# Revit family: Haworth_Morrison_Stool
name_source: partatom
category: Furniture
revit_build: Autodesk Revit 2018 (Build: 20170223_1515(x64)
units: mm (PartAtom-declared; Revit-internal decimal feet)

## family parameters
Always vertical = Yes
Cut with Voids When Loaded = No
OmniClass Number = 23.40.70.14.64.21
OmniClass Title = Systems Furniture
Room Calculation Point = No
Shared = No
Work Plane-Based = No

## types (3) — shared parameters
Actual Depth = 13 3/4"
Actual Width = 17 1/4"
Assembly Code = E2020200
Glide Finish = Haworth _ Polymer _ Slate
Manufacturer = Haworth
Model = HCCE-MSS
Revision Number = 7
Size = Verify Final Dim. w/ Haworth
URL = http://www.haworth.com
URL - Product = http://www.haworth.com
Warranty = http://www.haworth.com

## per-type parameters (varying)
| type | Actual Height | Description | High | Low | Medium | Seat Height |
| HCCE-MSS3 - High | 31" | Haworth Morrison Stool - High | Yes | No | No | 30 1/4" |
| HCCE-MSS2 - Medium | 27 1/2" | Haworth Morrison Stool - Medium | No | No | Yes | 26" |
| HCCE-MSS1 - Low | 17 3/4" | Haworth Morrison Stool - Low | No | Yes | No | 16 1/4" |

## geometry (parser evidence)
native form markers: Sweep x10
no freeform markers — native parametric forms only
